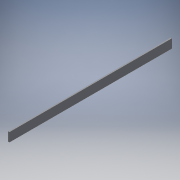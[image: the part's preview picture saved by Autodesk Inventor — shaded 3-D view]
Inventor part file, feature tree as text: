
AUTODESK INVENTOR PART (.ipt)
format: ipt  version: 2019 (Build 230136000, 136)  size: 93,184 bytes
history: native  units: in
note: dims shown in document units (in); Inventor stores cm internally (conversion verified against a paired STEP export)
features: extrude x1, sketch x1
ambient origin geometry x8: Origin, YZ Plane, XZ Plane, XY Plane, X Axis, Y Axis, Z Axis, Center Point
bodies: Solid1 (feature_tree)
feature tree (2):
  extrude  "Extrusion1"  Depth=5.25in
  sketch  "Sketch1"  dims[d0=96.0in d1=5.25in d2=0.75in d3=0.0in]
